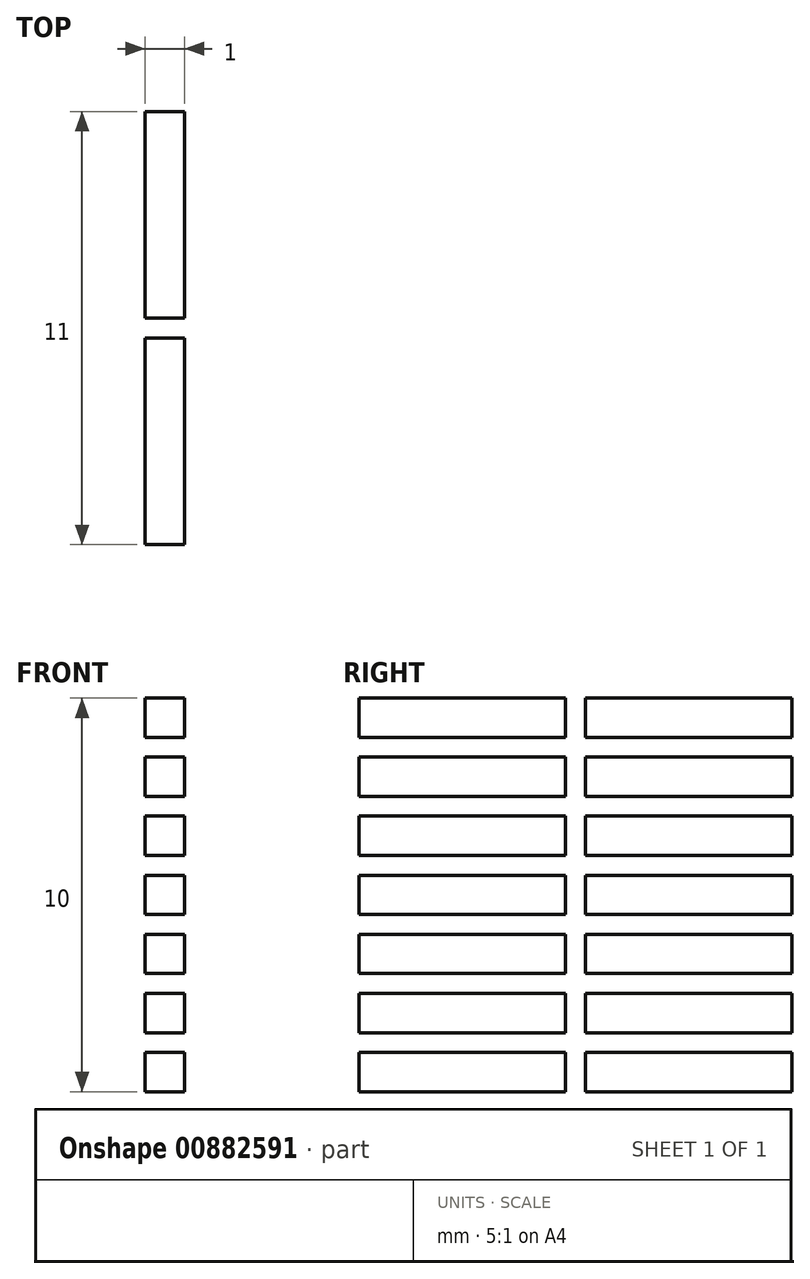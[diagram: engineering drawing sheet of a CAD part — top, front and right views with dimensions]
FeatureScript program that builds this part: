
annotation { "Feature Type Name" : "Feature", "Feature Type Description" : "" }
export const myFeature = defineFeature(function(context is Context, id is Id, definition is map)
    precondition{}
    {
        {
            var Q0;
            Q0=qCreatedBy(makeId("Right.planeOp"),FACE);
            var sketch = newSketch(context, id + "F0", { "sketchPlane" : qUnion([Q0])});
            skLineSegment(sketch, "E0.bottom", {"start": v(0, 0) * mm, "end": v(11.5, 0) * mm});
            skLineSegment(sketch, "E0.top", {"start": v(0, 11.5) * mm, "end": v(11.5, 11.5) * mm});
            skLineSegment(sketch, "E0.left", {"start": v(0, 0) * mm, "end": v(0, 11.5) * mm});
            skLineSegment(sketch, "E0.right", {"start": v(11.5, 0) * mm, "end": v(11.5, 11.5) * mm});
            skLineSegment(sketch, "E1.0", {"start": v(5.5, 11.5) * mm, "end": v(5.5, 10.25) * mm});
            skLineSegment(sketch, "E2.0", {"start": v(0, 11.25) * mm, "end": v(5.5, 11.25) * mm});
            skLineSegment(sketch, "E3", {"start": v(5.5, 11.25) * mm, "end": v(0.25, 11.25) * mm});
            skLineSegment(sketch, "E4", {"start": v(0.25, 11.25) * mm, "end": v(0.25, 10.25) * mm});
            skLineSegment(sketch, "E5", {"start": v(0.25, 10.25) * mm, "end": v(5.5, 10.25) * mm});
            skLineSegment(sketch, "E6.MirrorCS", {"start": v(0.25, 9.75) * mm, "end": v(5.5, 9.75) * mm});
            skLineSegment(sketch, "E7.MirrorCS", {"start": v(0.25, 8.75) * mm, "end": v(0.25, 9.75) * mm});
            skLineSegment(sketch, "E8.MirrorCS", {"start": v(5.5, 8.75) * mm, "end": v(0.25, 8.75) * mm});
            skLineSegment(sketch, "E9.MirrorCS", {"start": v(5.5, 8.75) * mm, "end": v(5.5, 9.75) * mm});
            skLineSegment(sketch, "E10.MirrorCS", {"start": v(5.5, 8.25) * mm, "end": v(0.25, 8.25) * mm});
            skLineSegment(sketch, "E11.MirrorCS", {"start": v(0.25, 8.25) * mm, "end": v(0.25, 7.25) * mm});
            skLineSegment(sketch, "E12.MirrorCS", {"start": v(0.25, 7.25) * mm, "end": v(5.5, 7.25) * mm});
            skLineSegment(sketch, "E13.MirrorCS", {"start": v(0.25, 6.75) * mm, "end": v(5.5, 6.75) * mm});
            skLineSegment(sketch, "E14.MirrorCS", {"start": v(0.25, 5.75) * mm, "end": v(0.25, 6.75) * mm});
            skLineSegment(sketch, "E15.MirrorCS", {"start": v(5.5, 5.75) * mm, "end": v(0.25, 5.75) * mm});
            skLineSegment(sketch, "E16.MirrorCS", {"start": v(5.5, 5.25) * mm, "end": v(0.25, 5.25) * mm});
            skLineSegment(sketch, "E17.MirrorCS", {"start": v(0.25, 5.25) * mm, "end": v(0.25, 4.25) * mm});
            skLineSegment(sketch, "E18.MirrorCS", {"start": v(0.25, 4.25) * mm, "end": v(5.5, 4.25) * mm});
            skLineSegment(sketch, "E19.MirrorCS", {"start": v(0.25, 3.75) * mm, "end": v(5.5, 3.75) * mm});
            skLineSegment(sketch, "E20.MirrorCS", {"start": v(0.25, 2.75) * mm, "end": v(0.25, 3.75) * mm});
            skLineSegment(sketch, "E21.MirrorCS", {"start": v(5.5, 2.75) * mm, "end": v(0.25, 2.75) * mm});
            skLineSegment(sketch, "E22.MirrorCS", {"start": v(5.5, 2.25) * mm, "end": v(0.25, 2.25) * mm});
            skLineSegment(sketch, "E23.MirrorCS", {"start": v(0.25, 2.25) * mm, "end": v(0.25, 1.25) * mm});
            skLineSegment(sketch, "E24.MirrorCS", {"start": v(0.25, 1.25) * mm, "end": v(5.5, 1.25) * mm});
            skLineSegment(sketch, "E25.trimOffspring", {"start": v(5.5, 8.25) * mm, "end": v(5.5, 7.25) * mm});
            skLineSegment(sketch, "E26.trimOffspring", {"start": v(5.5, 6.75) * mm, "end": v(5.5, 5.75) * mm});
            skLineSegment(sketch, "E27.trimOffspring", {"start": v(5.5, 5.25) * mm, "end": v(5.5, 4.25) * mm});
            skLineSegment(sketch, "E28.trimOffspring", {"start": v(5.5, 3.75) * mm, "end": v(5.5, 2.75) * mm});
            skLineSegment(sketch, "E29.trimOffspring", {"start": v(5.5, 2.25) * mm, "end": v(5.5, 1.25) * mm});
            skLineSegment(sketch, "E30.trimOffspring", {"start": v(5.5, 9.75) * mm, "end": v(5.5, 8.75) * mm});
            skLineSegment(sketch, "E31.MirrorCS", {"start": v(6, 11.25) * mm, "end": v(11.25, 11.25) * mm});
            skLineSegment(sketch, "E32.MirrorCS", {"start": v(11.25, 10.25) * mm, "end": v(6, 10.25) * mm});
            skLineSegment(sketch, "E33.MirrorCS", {"start": v(11.25, 11.25) * mm, "end": v(11.25, 10.25) * mm});
            skLineSegment(sketch, "E34.MirrorCS", {"start": v(11.25, 9.75) * mm, "end": v(6, 9.75) * mm});
            skLineSegment(sketch, "E35.MirrorCS", {"start": v(11.25, 8.75) * mm, "end": v(11.25, 9.75) * mm});
            skLineSegment(sketch, "E36.MirrorCS", {"start": v(6, 8.75) * mm, "end": v(11.25, 8.75) * mm});
            skLineSegment(sketch, "E37.MirrorCS", {"start": v(6, 8.75) * mm, "end": v(6, 9.75) * mm});
            skLineSegment(sketch, "E38.MirrorCS", {"start": v(6, 8.25) * mm, "end": v(11.25, 8.25) * mm});
            skLineSegment(sketch, "E39.MirrorCS", {"start": v(11.25, 8.25) * mm, "end": v(11.25, 7.25) * mm});
            skLineSegment(sketch, "E40.MirrorCS", {"start": v(11.25, 7.25) * mm, "end": v(6, 7.25) * mm});
            skLineSegment(sketch, "E41.MirrorCS", {"start": v(6, 8.25) * mm, "end": v(6, 7.25) * mm});
            skLineSegment(sketch, "E42.MirrorCS", {"start": v(11.25, 5.75) * mm, "end": v(11.25, 6.75) * mm});
            skLineSegment(sketch, "E43.MirrorCS", {"start": v(11.25, 6.75) * mm, "end": v(6, 6.75) * mm});
            skLineSegment(sketch, "E44.MirrorCS", {"start": v(6, 5.75) * mm, "end": v(11.25, 5.75) * mm});
            skLineSegment(sketch, "E45.MirrorCS", {"start": v(6, 6.75) * mm, "end": v(6, 5.75) * mm});
            skLineSegment(sketch, "E46.MirrorCS", {"start": v(6, 5.25) * mm, "end": v(6, 4.25) * mm});
            skLineSegment(sketch, "E47.MirrorCS", {"start": v(6, 5.25) * mm, "end": v(11.25, 5.25) * mm});
            skLineSegment(sketch, "E48.MirrorCS", {"start": v(11.25, 5.25) * mm, "end": v(11.25, 4.25) * mm});
            skLineSegment(sketch, "E49.MirrorCS", {"start": v(11.25, 4.25) * mm, "end": v(6, 4.25) * mm});
            skLineSegment(sketch, "E50.MirrorCS", {"start": v(11.25, 3.75) * mm, "end": v(6, 3.75) * mm});
            skLineSegment(sketch, "E51.MirrorCS", {"start": v(11.25, 2.75) * mm, "end": v(11.25, 3.75) * mm});
            skLineSegment(sketch, "E52.MirrorCS", {"start": v(6, 2.75) * mm, "end": v(11.25, 2.75) * mm});
            skLineSegment(sketch, "E53.MirrorCS", {"start": v(6, 3.75) * mm, "end": v(6, 2.75) * mm});
            skLineSegment(sketch, "E54.MirrorCS", {"start": v(6, 2.25) * mm, "end": v(11.25, 2.25) * mm});
            skLineSegment(sketch, "E55.MirrorCS", {"start": v(11.25, 2.25) * mm, "end": v(11.25, 1.25) * mm});
            skLineSegment(sketch, "E56.MirrorCS", {"start": v(11.25, 1.25) * mm, "end": v(6, 1.25) * mm});
            skLineSegment(sketch, "E57.MirrorCS", {"start": v(6, 2.25) * mm, "end": v(6, 1.25) * mm});
            skLineSegment(sketch, "E58", {"start": v(6, 10.25) * mm, "end": v(6, 11.25) * mm});
            skLineSegment(sketch, "E59.0", {"start": v(0.25, 0.75) * mm, "end": v(5.5, 0.75) * mm});
            skLineSegment(sketch, "E60", {"start": v(6, 1.25) * mm, "end": v(6, 0.75) * mm});
            skLineSegment(sketch, "E61", {"start": v(6, 0.75) * mm, "end": v(11.25, 0.75) * mm});
            skLineSegment(sketch, "E62", {"start": v(11.25, 0.75) * mm, "end": v(11.25, 0) * mm});
            skLineSegment(sketch, "E63", {"start": v(11.25, 0) * mm, "end": v(6, 0) * mm});
            skLineSegment(sketch, "E64", {"start": v(6, 0) * mm, "end": v(6, 0.75) * mm});
            skLineSegment(sketch, "E65", {"start": v(0.25, 0.75) * mm, "end": v(0.25, 0) * mm});
            skLineSegment(sketch, "E66", {"start": v(0.25, 0) * mm, "end": v(5.5, 0) * mm});
            skLineSegment(sketch, "E67", {"start": v(5.5, 0) * mm, "end": v(5.5, 0.75) * mm});
            skSolve(sketch);
        }
        {
            var Q0;
            {var subQ4=sQuery(id+"F0.wireOp",EDGE,"E4");Q0=makeQuery(id+"F0.imprint","IMPRINT",FACE,{"disambiguationData":[TD([[makeQuery(id+"F0.imprint","IMPRINT",EDGE,{"derivedFrom":subQ4}),1.0]])]});}
            var Q1;
            Q1=makeQuery(id+"F0.imprint","IMPRINT",FACE,{"disambiguationData":[TD([[makeQuery(id+"F0.imprint","IMPRINT",EDGE,{"derivedFrom":sQuery(id+"F0.wireOp",EDGE,"E31.MirrorCS")}),-1.0]])]});
            var Q2;
            Q2=makeQuery(id+"F0.imprint","IMPRINT",FACE,{"disambiguationData":[TD([[makeQuery(id+"F0.imprint","IMPRINT",EDGE,{"derivedFrom":sQuery(id+"F0.wireOp",EDGE,"E6.MirrorCS")}),-1.0]])]});
            var Q3;
            Q3=makeQuery(id+"F0.imprint","IMPRINT",FACE,{"disambiguationData":[TD([[makeQuery(id+"F0.imprint","IMPRINT",EDGE,{"derivedFrom":sQuery(id+"F0.wireOp",EDGE,"E34.MirrorCS")}),1.0]])]});
            var Q4;
            Q4=makeQuery(id+"F0.imprint","IMPRINT",FACE,{"disambiguationData":[TD([[makeQuery(id+"F0.imprint","IMPRINT",EDGE,{"derivedFrom":sQuery(id+"F0.wireOp",EDGE,"E10.MirrorCS")}),1.0]])]});
            var Q5;
            Q5=makeQuery(id+"F0.imprint","IMPRINT",FACE,{"disambiguationData":[TD([[makeQuery(id+"F0.imprint","IMPRINT",EDGE,{"derivedFrom":sQuery(id+"F0.wireOp",EDGE,"E38.MirrorCS")}),-1.0]])]});
            var Q6;
            Q6=makeQuery(id+"F0.imprint","IMPRINT",FACE,{"disambiguationData":[TD([[makeQuery(id+"F0.imprint","IMPRINT",EDGE,{"derivedFrom":sQuery(id+"F0.wireOp",EDGE,"E13.MirrorCS")}),-1.0]])]});
            var Q7;
            Q7=makeQuery(id+"F0.imprint","IMPRINT",FACE,{"disambiguationData":[TD([[makeQuery(id+"F0.imprint","IMPRINT",EDGE,{"derivedFrom":sQuery(id+"F0.wireOp",EDGE,"E42.MirrorCS")}),1.0]])]});
            var Q8;
            Q8=makeQuery(id+"F0.imprint","IMPRINT",FACE,{"disambiguationData":[TD([[makeQuery(id+"F0.imprint","IMPRINT",EDGE,{"derivedFrom":sQuery(id+"F0.wireOp",EDGE,"E16.MirrorCS")}),1.0]])]});
            var Q9;
            Q9=makeQuery(id+"F0.imprint","IMPRINT",FACE,{"disambiguationData":[TD([[makeQuery(id+"F0.imprint","IMPRINT",EDGE,{"derivedFrom":sQuery(id+"F0.wireOp",EDGE,"E46.MirrorCS")}),1.0]])]});
            var Q10;
            Q10=makeQuery(id+"F0.imprint","IMPRINT",FACE,{"disambiguationData":[TD([[makeQuery(id+"F0.imprint","IMPRINT",EDGE,{"derivedFrom":sQuery(id+"F0.wireOp",EDGE,"E50.MirrorCS")}),1.0]])]});
            var Q11;
            Q11=makeQuery(id+"F0.imprint","IMPRINT",FACE,{"disambiguationData":[TD([[makeQuery(id+"F0.imprint","IMPRINT",EDGE,{"derivedFrom":sQuery(id+"F0.wireOp",EDGE,"E19.MirrorCS")}),-1.0]])]});
            var Q12;
            Q12=makeQuery(id+"F0.imprint","IMPRINT",FACE,{"disambiguationData":[TD([[makeQuery(id+"F0.imprint","IMPRINT",EDGE,{"derivedFrom":sQuery(id+"F0.wireOp",EDGE,"E22.MirrorCS")}),1.0]])]});
            var Q13;
            Q13=makeQuery(id+"F0.imprint","IMPRINT",FACE,{"disambiguationData":[TD([[makeQuery(id+"F0.imprint","IMPRINT",EDGE,{"derivedFrom":sQuery(id+"F0.wireOp",EDGE,"E54.MirrorCS")}),-1.0]])]});
            extrude(context, id + "F1", {"entities" : qUnion([Q0, Q1, Q2, Q3, Q4, Q5, Q6, Q7, Q8, Q9, Q10, Q11, Q12, Q13]), "depth" : 1 * mm, "offsetDistance" : 25 * mm});
        }
    });
